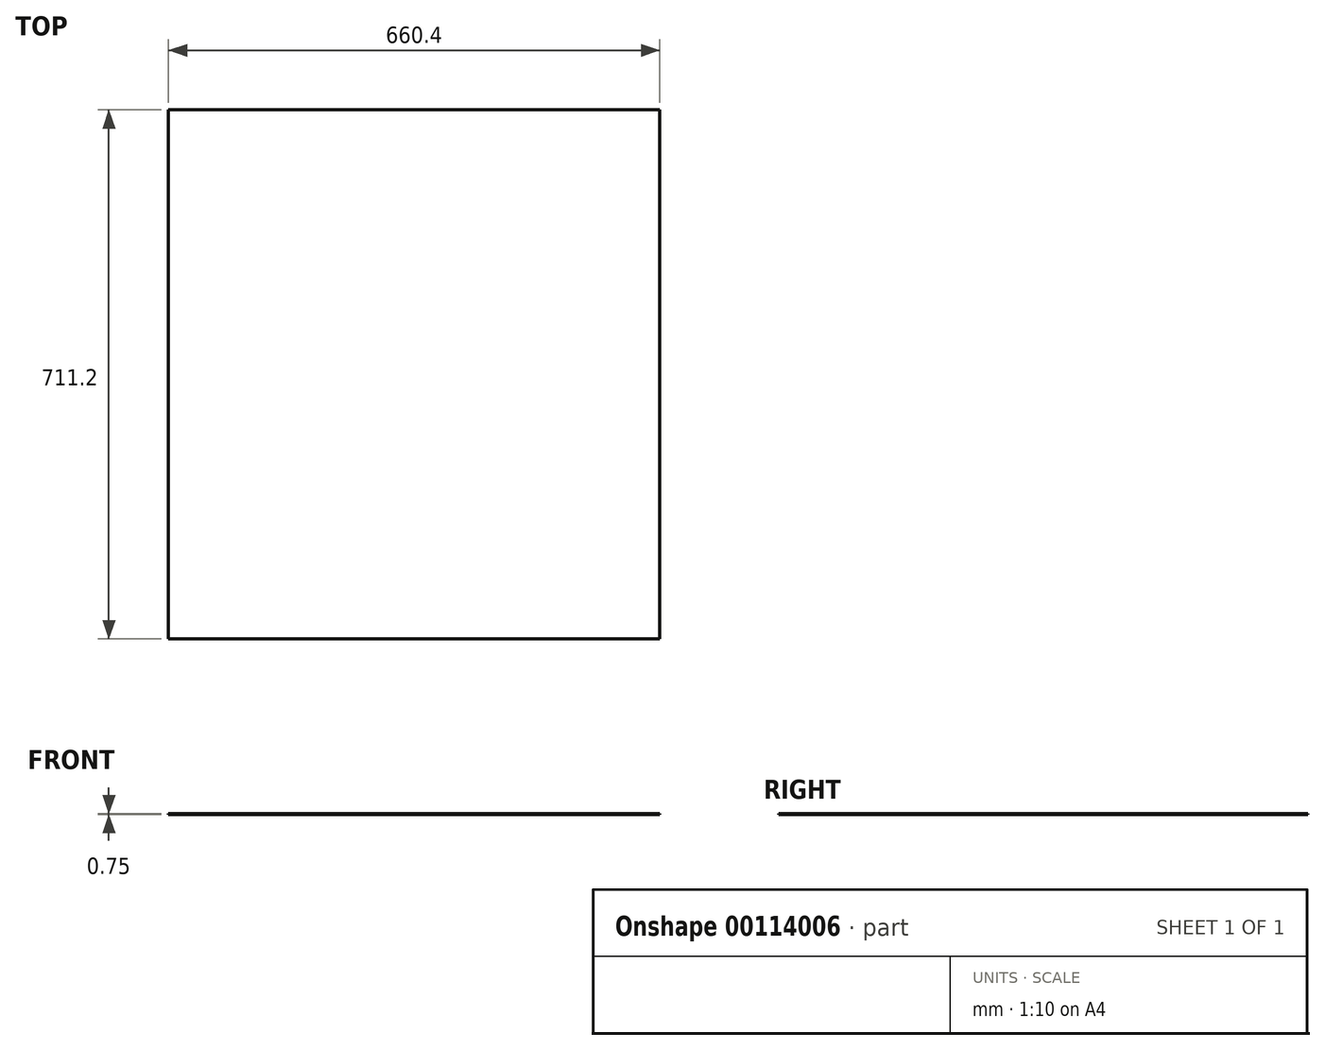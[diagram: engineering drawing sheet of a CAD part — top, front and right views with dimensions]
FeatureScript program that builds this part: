
annotation { "Feature Type Name" : "Feature", "Feature Type Description" : "" }
export const myFeature = defineFeature(function(context is Context, id is Id, definition is map)
    precondition{}
    {
        {
            assignVariable(context, id + "F0", {"name" : "thickness", "anyValue" : 3 / 4});
        }
        {
            var Q0;
            Q0=qCreatedBy(makeId("Top.planeOp"),FACE);
            var sketch = newSketch(context, id + "F1", { "sketchPlane" : qUnion([Q0])});
            skLineSegment(sketch, "E0.bottom", {"start": v(-330.2, 355.6) * mm, "end": v(330.2, 355.6) * mm});
            skLineSegment(sketch, "E0.top", {"start": v(-330.2, -355.6) * mm, "end": v(330.2, -355.6) * mm});
            skLineSegment(sketch, "E0.left", {"start": v(-330.2, 355.6) * mm, "end": v(-330.2, -355.6) * mm});
            skLineSegment(sketch, "E0.right", {"start": v(330.2, 355.6) * mm, "end": v(330.2, -355.6) * mm});
            skPoint(sketch, "E1", {"position": v(-330.2, 0) * mm});
            skPoint(sketch, "E2", {"position": v(0, 355.6) * mm});
            skLineSegment(sketch, "E3", {"start": v(0, 355.6) * mm, "end": v(0, 0) * mm, "construction": true});
            skLineSegment(sketch, "E4", {"start": v(0, 0) * mm, "end": v(-330.2, 0) * mm, "construction": true});
            skSolve(sketch);
        }
        {
            var Q0;
            Q0 = qSketchRegion(id + "F1", true);
            extrude(context, id + "F2", {"entities" : qUnion([Q0]), "depth" : (getVariable(context, 'thickness')) * mm});
        }
    });
